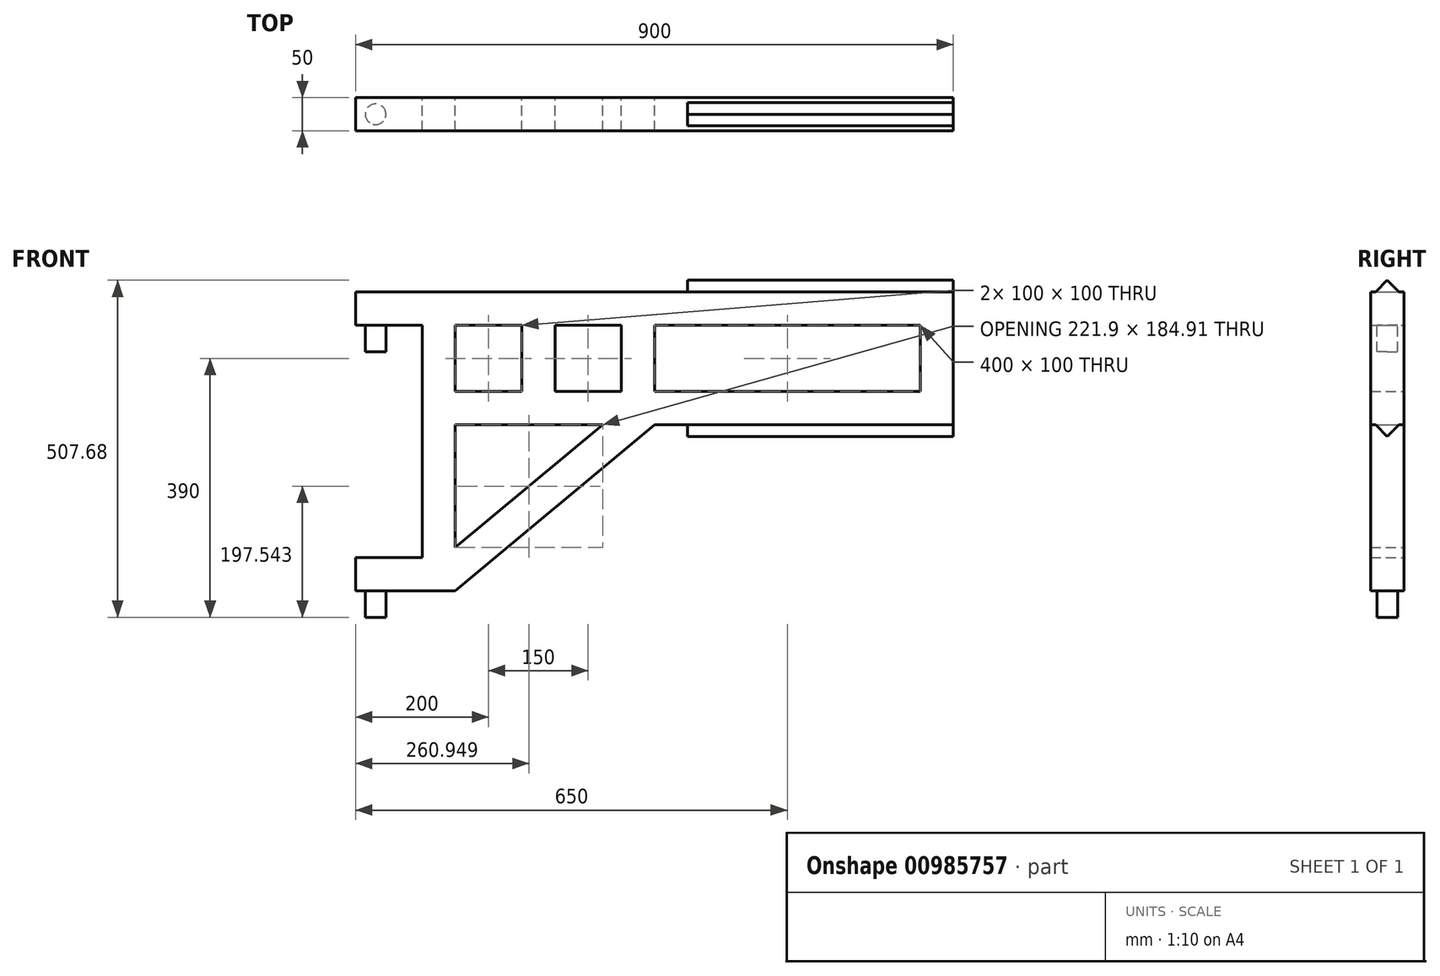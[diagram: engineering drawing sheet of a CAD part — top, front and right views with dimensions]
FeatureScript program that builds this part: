
annotation { "Feature Type Name" : "Feature", "Feature Type Description" : "" }
export const myFeature = defineFeature(function(context is Context, id is Id, definition is map)
    precondition{}
    {
        {
            var Q0;
            Q0=qCreatedBy(makeId("Front.planeOp"),FACE);
            var sketch = newSketch(context, id + "F0", { "sketchPlane" : qUnion([Q0])});
            skLineSegment(sketch, "E0.top", {"start": v(0, 200) * mm, "end": v(900, 200) * mm});
            skLineSegment(sketch, "E0.left", {"start": v(0, 150) * mm, "end": v(0, 200) * mm});
            skLineSegment(sketch, "E0.right", {"start": v(900, 0) * mm, "end": v(900, 200) * mm});
            skLineSegment(sketch, "E1.bottom", {"start": v(150, 150) * mm, "end": v(250, 150) * mm});
            skLineSegment(sketch, "E1.top", {"start": v(150, 50) * mm, "end": v(250, 50) * mm});
            skLineSegment(sketch, "E1.left", {"start": v(150, 150) * mm, "end": v(150, 50) * mm});
            skLineSegment(sketch, "E1.right", {"start": v(850, 150) * mm, "end": v(850, 50) * mm});
            skLineSegment(sketch, "E2.top", {"start": v(0, -250) * mm, "end": v(150, -250) * mm});
            skLineSegment(sketch, "E2.left", {"start": v(0, -200) * mm, "end": v(0, -250) * mm});
            skLineSegment(sketch, "E3.bottom", {"start": v(0, 150) * mm, "end": v(100, 150) * mm});
            skLineSegment(sketch, "E3.right", {"start": v(100, 150) * mm, "end": v(100, -200) * mm});
            skLineSegment(sketch, "E4.trimOffspring", {"start": v(450, 0) * mm, "end": v(900, 0) * mm});
            skLineSegment(sketch, "E5", {"start": v(0, -200) * mm, "end": v(100, -200) * mm});
            skPoint(sketch, "E0.bottom.start.orphan", {"position": v(0, 0) * mm});
            skLineSegment(sketch, "E6.left", {"start": v(400, 150) * mm, "end": v(400, 50) * mm});
            skLineSegment(sketch, "E6.right", {"start": v(450, 150) * mm, "end": v(450, 50) * mm});
            skLineSegment(sketch, "E7.left", {"start": v(250, 150) * mm, "end": v(250, 50) * mm});
            skLineSegment(sketch, "E7.right", {"start": v(300, 150) * mm, "end": v(300, 50) * mm});
            skLineSegment(sketch, "E8.trimOffspring", {"start": v(300, 150) * mm, "end": v(400, 150) * mm});
            skLineSegment(sketch, "E9.trimOffspring", {"start": v(300, 50) * mm, "end": v(400, 50) * mm});
            skLineSegment(sketch, "E10.trimOffspring", {"start": v(450, 150) * mm, "end": v(850, 150) * mm});
            skLineSegment(sketch, "E11.trimOffspring", {"start": v(450, 50) * mm, "end": v(850, 50) * mm});
            skLineSegment(sketch, "E12", {"start": v(150, 0) * mm, "end": v(150, -184.91) * mm});
            skLineSegment(sketch, "E13", {"start": v(371.9, 0) * mm, "end": v(150, 0) * mm});
            skLineSegment(sketch, "E14", {"start": v(150, -250) * mm, "end": v(450, 0) * mm});
            skLineSegment(sketch, "E15", {"start": v(150, -184.91) * mm, "end": v(371.9, 0) * mm});
            skPoint(sketch, "E16.orphan", {"position": v(150, -200) * mm});
            skSolve(sketch);
        }
        {
            var Q0;
            Q0=makeQuery(id+"F0.imprint","IMPRINT",FACE,{"disambiguationData":[TD([[makeQuery(id+"F0.imprint","IMPRINT",EDGE,{"derivedFrom":sQuery(id+"F0.wireOp",EDGE,"E0.top")}),-1.0]])]});
            extrude(context, id + "F1", {"entities" : qUnion([Q0]), "endBound" : BoundingType.SYMMETRIC, "depth" : 50 * mm, "offsetDistance" : 25 * mm});
        }
        {
            var Q0;
            Q0=makeQuery(id+"F1.opExtrude","SWEPT_FACE",FACE,{"disambiguationData":[OSD([sQuery(id+"F0.wireOp",EDGE,"E0.right")])]});
            var sketch = newSketch(context, id + "F2", { "sketchPlane" : qUnion([Q0])});
            skLineSegment(sketch, "E17", {"start": v(-17.68, 0) * mm, "end": v(0, -17.68) * mm});
            skLineSegment(sketch, "E18", {"start": v(0, -17.68) * mm, "end": v(17.68, 0) * mm});
            skLineSegment(sketch, "E19", {"start": v(-17.68, 200) * mm, "end": v(0, 217.68) * mm});
            skLineSegment(sketch, "E20", {"start": v(0, 217.68) * mm, "end": v(17.68, 200) * mm});
            skSolve(sketch);
        }
        {
            var Q0;
            {var subQ0=sQuery(id+"F2.wireOp",EDGE,"E19");Q0=makeQuery(id+"F2.imprint","IMPRINT",FACE,{"disambiguationData":[TD([[makeQuery(id+"F2.imprint","IMPRINT",EDGE,{"derivedFrom":subQ0}),-1.0]])]});}
            var Q1;
            {var subQ0=sQuery(id+"F2.wireOp",EDGE,"E17");Q1=makeQuery(id+"F2.imprint","IMPRINT",FACE,{"disambiguationData":[TD([[makeQuery(id+"F2.imprint","IMPRINT",EDGE,{"derivedFrom":subQ0}),1.0]])]});}
            extrude(context, id + "F3", {"entities" : qUnion([Q0, Q1]), "operationType" : NewBodyOperationType.ADD, "oppositeDirection" : true, "depth" : 400 * mm, "offsetDistance" : 25 * mm});
        }
        {
            var Q0;
            Q0=makeQuery(id+"F1.opExtrude","SWEPT_FACE",FACE,{"disambiguationData":[OSD([sQuery(id+"F0.wireOp",EDGE,"E3.bottom")])]});
            var sketch = newSketch(context, id + "F4", { "sketchPlane" : qUnion([Q0])});
            skCircle(sketch, "E21", {"center": v(30, 0) * mm, "radius": 15.5 * mm});
            skSolve(sketch);
        }
        {
            var Q0;
            Q0=makeQuery(id+"F1.opExtrude","SWEPT_FACE",FACE,{"disambiguationData":[OSD([sQuery(id+"F0.wireOp",EDGE,"E2.top")])]});
            var sketch = newSketch(context, id + "F5", { "sketchPlane" : qUnion([Q0])});
            skCircle(sketch, "E22", {"center": v(30, 0) * mm, "radius": 15.5 * mm});
            skSolve(sketch);
        }
        {
            var Q0;
            Q0=makeQuery(id+"F4.imprint","IMPRINT",FACE,{"disambiguationData":[TD([[makeQuery(id+"F4.imprint","IMPRINT",EDGE,{"derivedFrom":sQuery(id+"F4.wireOp",EDGE,"E21")}),1.0]])]});
            extrude(context, id + "F6", {"entities" : qUnion([Q0]), "operationType" : NewBodyOperationType.ADD, "depth" : 40 * mm, "offsetDistance" : 25 * mm});
        }
        {
            var Q0;
            Q0=makeQuery(id+"F5.imprint","IMPRINT",FACE,{"disambiguationData":[TD([[makeQuery(id+"F5.imprint","IMPRINT",EDGE,{"derivedFrom":sQuery(id+"F5.wireOp",EDGE,"E22")}),1.0]])]});
            extrude(context, id + "F7", {"entities" : qUnion([Q0]), "operationType" : NewBodyOperationType.ADD, "depth" : 40 * mm, "offsetDistance" : 25 * mm});
        }
    });
